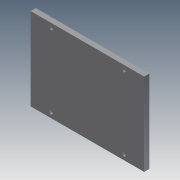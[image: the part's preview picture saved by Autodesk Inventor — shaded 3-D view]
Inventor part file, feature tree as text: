
AUTODESK INVENTOR PART (.ipt)
format: ipt  version: 2011 (Build 150239000, 239)  size: 177,664 bytes
history: native  units: in
note: dims shown in document units (in); Inventor stores cm internally (conversion verified against a paired STEP export)
features: extrude x12, sketch x12, fillet x1
ambient origin geometry x8: Origin, YZ Plane, XZ Plane, XY Plane, X Axis, Y Axis, Z Axis, Center Point
bodies: Solid1 (feature_tree)
feature tree (25):
  extrude  "Extrusion1"  Depth=4.0in
  extrude  "Extrusion2"  Depth=2.16in
  extrude  "Extrusion3"  Depth=1.7655in
  extrude  "Extrusion4"  Depth=0.029in TaperAngle=0.0deg
  extrude  "Extrusion5"  Depth=2.36in
  fillet  "Fillet1"  Radius=2.56in
  extrude  "Extrusion6"  Depth=0.125in
  extrude  "Extrusion7"  Depth=0.25in TaperAngle=0.0deg
  extrude  "Extrusion8"  Depth=0.25in
  extrude  "Extrusion9"  Depth=1.0in TaperAngle=0.0deg
  extrude  "Extrusion10"  Depth=0.25in TaperAngle=0.0deg
  extrude  "Extrusion11"  Depth=0.75in TaperAngle=0.0deg
  extrude  "Extrusion12"  [1 undecoded]
  sketch  "Sketch1"  dims[d0=4.0in d1=4.0in]
  sketch  "Sketch2"  dims[d2=0.029in d3=0.0in d4=2.16in]
  sketch  "Sketch3"  dims[d5=0.029in d6=0.0in d7=1.7655in]
  sketch  "Sketch4"  dims[d8=0.156in d9=0.029in d10=0.0in]
  sketch  "Sketch5"  dims[d11=0.029in d12=0.0in d13=2.36in d14=2.56in]
  sketch  "Sketch6"  dims[d15=0.262in d16=0.0in d17=0.125in]
  sketch  "Sketch7"  dims[d18=0.25in d19=0.0in d20=0.25in d21=0.0in]
  sketch  "Sketch8"  dims[d22=0.25in d23=0.25in]
  sketch  "Sketch9"  dims[d24=0.5in d25=1.0in d26=0.0in]
  sketch  "Sketch10"  dims[d27=1.0in d28=0.0in d29=0.25in d30=0.0in]
  sketch  "Sketch11"  dims[d31=0.75in d32=0.0in d33=0.75in d34=0.0in]
  sketch  "Sketch12"
note: 1 required parameter value undecoded (feature->parameter linkage not recoverable at this tier; creation-order binding heuristic only, values carry confidence <= 0.55)
